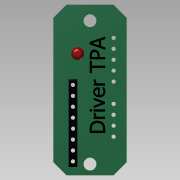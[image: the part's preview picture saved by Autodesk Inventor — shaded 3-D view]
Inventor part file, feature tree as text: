
AUTODESK INVENTOR PART (.ipt)
format: ipt  version: 2015 SP1 (Build 190203100, 203)  size: 187,392 bytes
history: native  units: mm
features: extrude x7, sketch x2, fillet x1
ambient origin geometry x8: Origin, YZ Plane, XZ Plane, XY Plane, X Axis, Y Axis, Z Axis, Center Point
bodies: Solid1 (feature_tree)
feature tree (10):
  sketch  "Sketch1"  dims[d0=17.0mm d1=39.65mm]
  extrude  "Extrusion2"  Depth=39.65mm
  extrude  "Extrusion3"  Depth=10.0mm
  extrude  "Extrusion4"  Depth=10.0mm
  extrude  "Extrusion5"  Depth=10.0mm
  fillet  "Fillet1"  Radius=3.0mm
  sketch  "Sketch2"  dims[d2=3.0mm d3=3.0mm d4=3.0mm d5=3.0mm d6=3.0mm d7=3.0mm d8=3.0mm d9=3.0mm d10=1.0mm d11=1.0mm d12=1.0mm d13=1.0mm d14=1.0mm d15=1.0mm d16=1.0mm d17=2.54mm d18=2.54mm d19=2.54mm d20=2.54mm d21=2.54mm d23=3.0mm d24=1.0mm d25=1.0mm d26=1.0mm d27=1.0mm d28=2.54mm d29=2.54mm d30=2.54mm d31=1.0mm d32=1.0mm d33=1.0mm d34=1.0mm d35=2.54mm d36=2.54mm d37=2.54mm d39=2.54mm d42=8.4mm d43=0.0mm d44=5.0mm d45=0.0mm d46=1.7mm d47=0.0mm d48=1.7mm d49=0.0mm d50=1.0mm d51=3.0mm d52=3.0mm d53=2.6mm d54=3.72mm d55=10.0mm d56=0.0mm d57=10.0mm d58=0.0mm d59=33.33mm d60=1.0mm d61=2.54mm d62=2.54mm d63=1.330315mm d64=1.330315mm d65=10.0mm d66=0.0mm]
  extrude  "Extrusion6"  Depth=10.0mm
  extrude  "Extrusion7"  Depth=10.0mm
  extrude  "Extrusion8"  Depth=10.0mm
